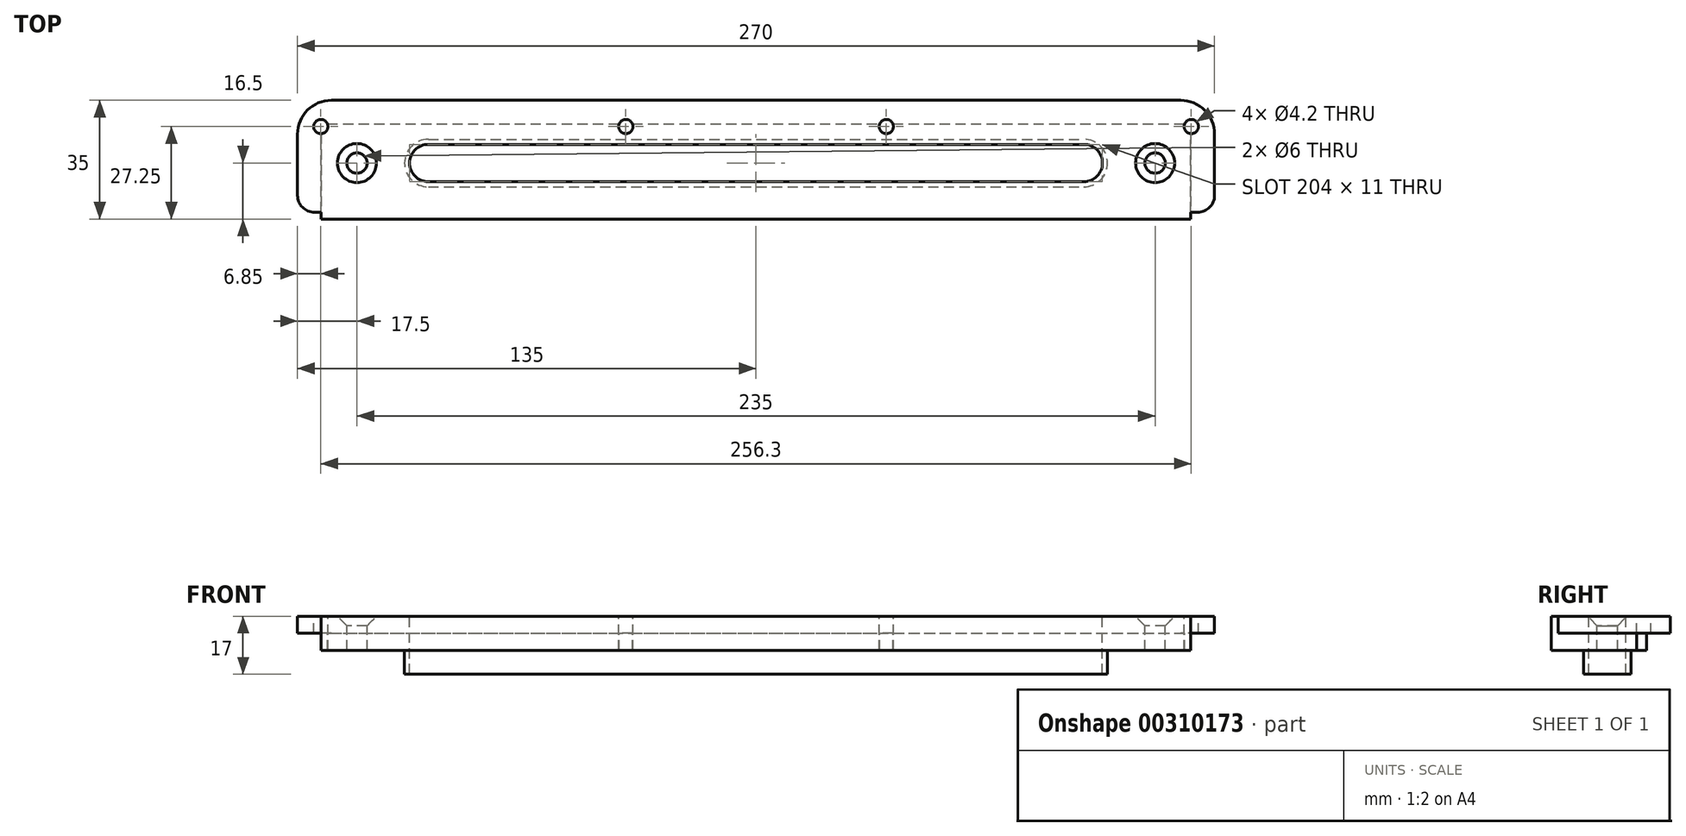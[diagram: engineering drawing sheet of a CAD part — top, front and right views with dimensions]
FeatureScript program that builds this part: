
annotation { "Feature Type Name" : "Feature", "Feature Type Description" : "" }
export const myFeature = defineFeature(function(context is Context, id is Id, definition is map)
    precondition{}
    {
        {
            var Q0;
            Q0=qCreatedBy(makeId("Top.planeOp"),FACE);
            var sketch = newSketch(context, id + "F0", { "sketchPlane" : qUnion([Q0])});
            skArc(sketch, "E0", {"start": v(-96.5, 5.5) * mm, "mid": v(-102, 0) * mm, "end": v(-96.5, -5.5) * mm});
            skArc(sketch, "E1.MirrorC", {"start": v(96.5, 5.5) * mm, "mid": v(102, 0) * mm, "end": v(96.5, -5.5) * mm});
            skLineSegment(sketch, "E2", {"start": v(-96.5, 5.5) * mm, "end": v(96.5, 5.5) * mm});
            skLineSegment(sketch, "E3", {"start": v(-96.5, -5.5) * mm, "end": v(96.5, -5.5) * mm});
            skArc(sketch, "E4", {"start": v(-125, 18.5) * mm, "mid": v(-132.07, 15.57) * mm, "end": v(-135, 8.5) * mm});
            skArc(sketch, "E5.MirrorC", {"start": v(125, 18.5) * mm, "mid": v(132.07, 15.57) * mm, "end": v(135, 8.5) * mm});
            skLineSegment(sketch, "E6", {"start": v(-125, 18.5) * mm, "end": v(125, 18.5) * mm});
            skLineSegment(sketch, "E7", {"start": v(-135, 8.5) * mm, "end": v(-135, -9.5) * mm});
            skLineSegment(sketch, "E8.MirrorCS", {"start": v(135, 8.5) * mm, "end": v(135, -9.5) * mm});
            skArc(sketch, "E9", {"start": v(-135, -9.5) * mm, "mid": v(-133.54, -13.04) * mm, "end": v(-130, -14.5) * mm});
            skArc(sketch, "E10.MirrorC", {"start": v(135, -9.5) * mm, "mid": v(133.54, -13.04) * mm, "end": v(130, -14.5) * mm});
            skLineSegment(sketch, "E11", {"start": v(-130, -14.5) * mm, "end": v(-128, -14.5) * mm});
            skLineSegment(sketch, "E12", {"start": v(-128, -14.5) * mm, "end": v(-128, -16.5) * mm});
            skLineSegment(sketch, "E13.MirrorCS", {"start": v(130, -14.5) * mm, "end": v(128, -14.5) * mm});
            skLineSegment(sketch, "E14.MirrorCS", {"start": v(128, -14.5) * mm, "end": v(128, -16.5) * mm});
            skLineSegment(sketch, "E15", {"start": v(-128, -16.5) * mm, "end": v(128, -16.5) * mm});
            skCircle(sketch, "E16", {"center": v(-117.5, 0) * mm, "radius": 5.5 * mm, "construction": true});
            skCircle(sketch, "E17.MirrorC", {"center": v(117.5, 0) * mm, "radius": 5.5 * mm, "construction": true});
            skCircle(sketch, "E18", {"center": v(-38.35, 10.75) * mm, "radius": 2.75 * mm, "construction": true});
            skCircle(sketch, "E19", {"center": v(-128.15, 10.75) * mm, "radius": 2.75 * mm, "construction": true});
            skCircle(sketch, "E20.MirrorC", {"center": v(38.35, 10.75) * mm, "radius": 2.75 * mm, "construction": true});
            skCircle(sketch, "E21.MirrorC", {"center": v(128.15, 10.75) * mm, "radius": 2.75 * mm, "construction": true});
            skLineSegment(sketch, "E22", {"start": v(-128, -14.5) * mm, "end": v(-128, 11.5) * mm});
            skLineSegment(sketch, "E23.MirrorCS", {"start": v(128, -14.5) * mm, "end": v(128, 11.5) * mm});
            skLineSegment(sketch, "E24", {"start": v(-128, 11.5) * mm, "end": v(128, 11.5) * mm});
            skLineSegment(sketch, "E25.0", {"start": v(-96.5, -7) * mm, "end": v(96.5, -7) * mm});
            skArc(sketch, "E25.1", {"start": v(-96.5, 7) * mm, "mid": v(-103.5, 0) * mm, "end": v(-96.5, -7) * mm});
            skLineSegment(sketch, "E25.2", {"start": v(-96.5, 7) * mm, "end": v(96.5, 7) * mm});
            skArc(sketch, "E25.3", {"start": v(96.5, 7) * mm, "mid": v(103.5, 0) * mm, "end": v(96.5, -7) * mm});
            skSolve(sketch);
        }
        {
            var Q0;
            Q0=makeQuery(id+"F0.imprint","IMPRINT",FACE,{"disambiguationData":[TD([[makeQuery(id+"F0.imprint","IMPRINT",EDGE,{"derivedFrom":sQuery(id+"F0.wireOp",EDGE,"E0")}),-1.0]])]});
            extrude(context, id + "F1", {"entities" : qUnion([Q0]), "oppositeDirection" : true, "depth" : 17 * mm});
        }
        {
            var Q0;
            Q0=makeQuery(id+"F0.imprint","IMPRINT",FACE,{"disambiguationData":[TD([[makeQuery(id+"F0.imprint","IMPRINT",EDGE,{"derivedFrom":sQuery(id+"F0.wireOp",EDGE,"E12")}),1.0]])]});
            extrude(context, id + "F2", {"entities" : qUnion([Q0]), "operationType" : NewBodyOperationType.ADD, "oppositeDirection" : true, "depth" : 10 * mm});
        }
        {
            var Q0;
            Q0=makeQuery(id+"F0.imprint","IMPRINT",FACE,{"disambiguationData":[TD([[makeQuery(id+"F0.imprint","IMPRINT",EDGE,{"derivedFrom":sQuery(id+"F0.wireOp",EDGE,"E4")}),1.0]])]});
            extrude(context, id + "F3", {"entities" : qUnion([Q0]), "operationType" : NewBodyOperationType.ADD, "oppositeDirection" : true, "depth" : 5 * mm});
        }
        {
            var Q0;
            Q0=sQuery(id+"F0.wireOp",VERTEX,"E17.MirrorC.center");
            var Q1;
            Q1=sQuery(id+"F0.wireOp",VERTEX,"E16.center");
            var Q2;
            Q2=makeQuery(id+"F1.opExtrude","SWEPT_BODY",BODY,{"disambiguationData":[OSD([sQuery(id+"F0.wireOp",EDGE,"E0"),sQuery(id+"F0.wireOp",EDGE,"E1.MirrorC"),sQuery(id+"F0.wireOp",EDGE,"E2"),sQuery(id+"F0.wireOp",EDGE,"E3"),sQuery(id+"F0.wireOp",EDGE,"E25.0"),sQuery(id+"F0.wireOp",EDGE,"E25.1"),sQuery(id+"F0.wireOp",EDGE,"E25.2"),sQuery(id+"F0.wireOp",EDGE,"E25.3")])]});
            hole(context, id + "F4", {"style" : HoleStyle.C_SINK, "endStyle" : HoleEndStyle.THROUGH, "holeDiameter" : 6 * mm, "cSinkDiameter" : 11.5 * mm, "cSinkAngle" : 90 * degree, "tappedDepth" : 12 * mm, "tapClearance" : 3, "locations" : qUnion([Q0, Q1]), "scope" : qUnion([Q2])});
        }
        {
            var Q0;
            Q0=sQuery(id+"F0.wireOp",VERTEX,"E19.center");
            var Q1;
            Q1=sQuery(id+"F0.wireOp",VERTEX,"E18.center");
            var Q2;
            Q2=sQuery(id+"F0.wireOp",VERTEX,"E20.MirrorC.center");
            var Q3;
            Q3=sQuery(id+"F0.wireOp",VERTEX,"E21.MirrorC.center");
            var Q4;
            Q4=makeQuery(id+"F1.opExtrude","SWEPT_BODY",BODY,{"disambiguationData":[OSD([sQuery(id+"F0.wireOp",EDGE,"E0"),sQuery(id+"F0.wireOp",EDGE,"E1.MirrorC"),sQuery(id+"F0.wireOp",EDGE,"E2"),sQuery(id+"F0.wireOp",EDGE,"E3"),sQuery(id+"F0.wireOp",EDGE,"E25.0"),sQuery(id+"F0.wireOp",EDGE,"E25.1"),sQuery(id+"F0.wireOp",EDGE,"E25.2"),sQuery(id+"F0.wireOp",EDGE,"E25.3")])]});
            hole(context, id + "F5", {"style" : HoleStyle.SIMPLE, "endStyle" : HoleEndStyle.THROUGH, "standardTappedOrClearance" : lookupTablePath({ "standard" : "ISO", "engagement" : "75%", "pitch" : "0.8 mm", "size" : "M5", "type" : "Tapped" }), "standardBlindInLast" : lookupTablePath({ "standard" : "ISO", "engagement" : "75%", "pitch" : "0.8 mm", "size" : "M5", "type" : "Tapped" }), "holeDiameter" : 4.2 * mm, "showTappedDepth" : true, "tappedDepth" : 12 * mm, "tapClearance" : 3, "locations" : qUnion([Q0, Q1, Q2, Q3]), "scope" : qUnion([Q4]), "majorDiameter" : 5 * mm});
        }
    });
